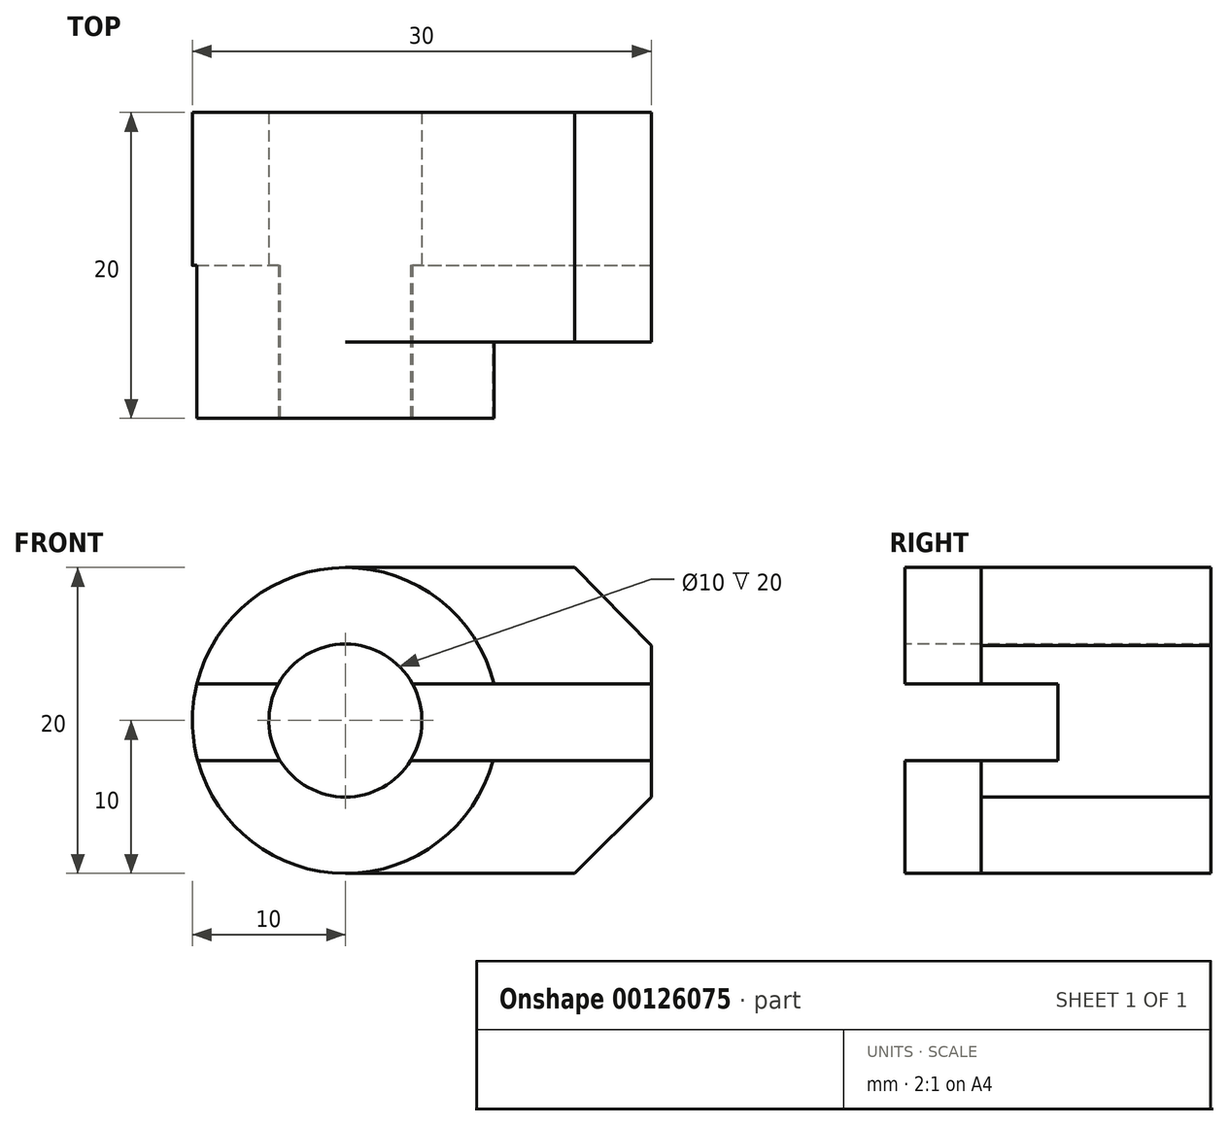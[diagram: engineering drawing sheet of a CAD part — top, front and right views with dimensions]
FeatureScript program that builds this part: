
annotation { "Feature Type Name" : "Feature", "Feature Type Description" : "" }
export const myFeature = defineFeature(function(context is Context, id is Id, definition is map)
    precondition{}
    {
        {
            var Q0;
            Q0=qCreatedBy(makeId("Top.planeOp"),FACE);
            var sketch = newSketch(context, id + "F0", { "sketchPlane" : qUnion([Q0])});
            skLineSegment(sketch, "E0.bottom", {"start": v(0, 5) * mm, "end": v(30, 5) * mm});
            skLineSegment(sketch, "E0.top", {"start": v(0, 20) * mm, "end": v(30, 20) * mm});
            skLineSegment(sketch, "E0.left", {"start": v(0, 5) * mm, "end": v(0, 20) * mm});
            skLineSegment(sketch, "E0.right", {"start": v(30, 5) * mm, "end": v(30, 20) * mm});
            skSolve(sketch);
        }
        {
            var Q0;
            Q0=makeQuery(id+"F0.imprint","IMPRINT",FACE,{"disambiguationData":[TD([[makeQuery(id+"F0.imprint","IMPRINT",EDGE,{"derivedFrom":sQuery(id+"F0.wireOp",EDGE,"E0.bottom")}),1.0]])]});
            extrude(context, id + "F1", {"entities" : qUnion([Q0]), "depth" : 20 * mm});
        }
        {
            var Q0;
            Q0=makeQuery(id+"F1.opExtrude","SWEPT_FACE",FACE,{"disambiguationData":[OSD([sQuery(id+"F0.wireOp",EDGE,"E0.bottom")])]});
            var sketch = newSketch(context, id + "F2", { "sketchPlane" : qUnion([Q0])});
            skLineSegment(sketch, "E1", {"start": v(30, 20) * mm, "end": v(25, 20) * mm});
            skLineSegment(sketch, "E2", {"start": v(25, 20) * mm, "end": v(30, 14.9) * mm});
            skLineSegment(sketch, "E3", {"start": v(30, 14.9) * mm, "end": v(30, 20) * mm});
            skLineSegment(sketch, "E4", {"start": v(30, 0) * mm, "end": v(30, 5) * mm});
            skLineSegment(sketch, "E5", {"start": v(30, 5) * mm, "end": v(25, 0) * mm});
            skLineSegment(sketch, "E6", {"start": v(25, 0) * mm, "end": v(30, 0) * mm});
            skCircle(sketch, "E7", {"center": v(10, 10) * mm, "radius": 10 * mm});
            skPoint(sketch, "E7.centerSnap0", {"position": v(0, 10) * mm});
            skCircle(sketch, "E8", {"center": v(10, 10) * mm, "radius": 5 * mm});
            skSolve(sketch);
        }
        {
            var Q0;
            Q0=makeQuery(id+"F2.imprint","IMPRINT",FACE,{"disambiguationData":[TD([[makeQuery(id+"F2.imprint","IMPRINT",EDGE,{"derivedFrom":sQuery(id+"F2.wireOp",EDGE,"E1")}),-1.0]])]});
            var Q1;
            Q1=makeQuery(id+"F2.imprint","IMPRINT",FACE,{"disambiguationData":[TD([[makeQuery(id+"F2.imprint","IMPRINT",EDGE,{"derivedFrom":sQuery(id+"F2.wireOp",EDGE,"E4")}),-1.0]])]});
            extrude(context, id + "F3", {"entities" : qUnion([Q0, Q1]), "operationType" : NewBodyOperationType.REMOVE, "endBound" : BoundingType.THROUGH_ALL, "oppositeDirection" : true, "depth" : 25 * mm});
        }
        {
            var Q0;
            Q0=makeQuery(id+"F2.imprint","IMPRINT",FACE,{"disambiguationData":[TD([[makeQuery(id+"F2.imprint","IMPRINT",EDGE,{"derivedFrom":sQuery(id+"F2.wireOp",EDGE,"E8")}),1.0]])]});
            extrude(context, id + "F4", {"entities" : qUnion([Q0]), "operationType" : NewBodyOperationType.REMOVE, "endBound" : BoundingType.THROUGH_ALL, "oppositeDirection" : true, "depth" : 25 * mm});
        }
        {
            var Q0;
            Q0=makeQuery(id+"F2.imprint","IMPRINT",FACE,{"disambiguationData":[TD([[makeQuery(id+"F2.imprint","IMPRINT",EDGE,{"derivedFrom":sQuery(id+"F2.wireOp",EDGE,"E8")}),-1.0]])]});
            extrude(context, id + "F5", {"entities" : qUnion([Q0]), "operationType" : NewBodyOperationType.ADD, "depth" : 5 * mm});
        }
        {
            var Q0;
            Q0=makeQuery(id+"F1.opExtrude","SWEPT_FACE",FACE,{"disambiguationData":[OSD([sQuery(id+"F0.wireOp",EDGE,"E0.right")])]});
            var sketch = newSketch(context, id + "F6", { "sketchPlane" : qUnion([Q0])});
            skLineSegment(sketch, "E9.bottom", {"start": v(0, 12.4) * mm, "end": v(10, 12.4) * mm});
            skLineSegment(sketch, "E9.top", {"start": v(0, 7.4) * mm, "end": v(10, 7.4) * mm});
            skLineSegment(sketch, "E9.left", {"start": v(0, 12.4) * mm, "end": v(0, 7.4) * mm});
            skLineSegment(sketch, "E9.right", {"start": v(10, 12.4) * mm, "end": v(10, 7.4) * mm});
            skSolve(sketch);
        }
        {
            var Q0;
            Q0 = qSketchRegion(id + "F6", true);
            extrude(context, id + "F7", {"entities" : qUnion([Q0]), "operationType" : NewBodyOperationType.REMOVE, "endBound" : BoundingType.THROUGH_ALL, "oppositeDirection" : true, "depth" : 25 * mm});
        }
        {
            var Q0;
            {var subQ0=sQuery(id+"F0.wireOp",EDGE,"E0.bottom");var subQ1=makeQuery(id+"F1.opExtrude","SWEPT_FACE",FACE,{"disambiguationData":[OSD([subQ0])]});var subQ2=sQuery(id+"F0.wireOp",EDGE,"E0.left");Q0=makeQuery(id+"F5.boolean.opBoolean","SPLIT",FACE,{"disambiguationData":[TD([subQ1,makeQuery(id+"F1.opExtrude","CAP_FACE",FACE,{"disambiguationData":[OSD([subQ0,sQuery(id+"F0.wireOp",EDGE,"E0.top"),subQ2,sQuery(id+"F0.wireOp",EDGE,"E0.right")])],"isStart":false}),makeQuery(id+"F1.opExtrude","SWEPT_FACE",FACE,{"disambiguationData":[OSD([subQ2])]}),makeQuery(id+"F5.opExtrude","SWEPT_FACE",FACE,{"disambiguationData":[OSD([sQuery(id+"F2.wireOp",EDGE,"E7")])]})])],"derivedFrom":subQ1});}
            var sketch = newSketch(context, id + "F8", { "sketchPlane" : qUnion([Q0])});
            skLineSegment(sketch, "E10", {"start": v(0, 0) * mm, "end": v(0, 20) * mm});
            skLineSegment(sketch, "E11", {"start": v(0, 20) * mm, "end": v(10, 20) * mm});
            skLineSegment(sketch, "E12", {"start": v(0, 0) * mm, "end": v(10, 0) * mm});
            skArc(sketch, "E13", {"start": v(10, 20) * mm, "mid": v(0, 10) * mm, "end": v(10, 0) * mm});
            skSolve(sketch);
        }
        {
            var Q0;
            Q0 = qSketchRegion(id + "F8", true);
            extrude(context, id + "F9", {"entities" : qUnion([Q0]), "operationType" : NewBodyOperationType.REMOVE, "endBound" : BoundingType.THROUGH_ALL, "oppositeDirection" : true, "depth" : 25 * mm});
        }
    });
